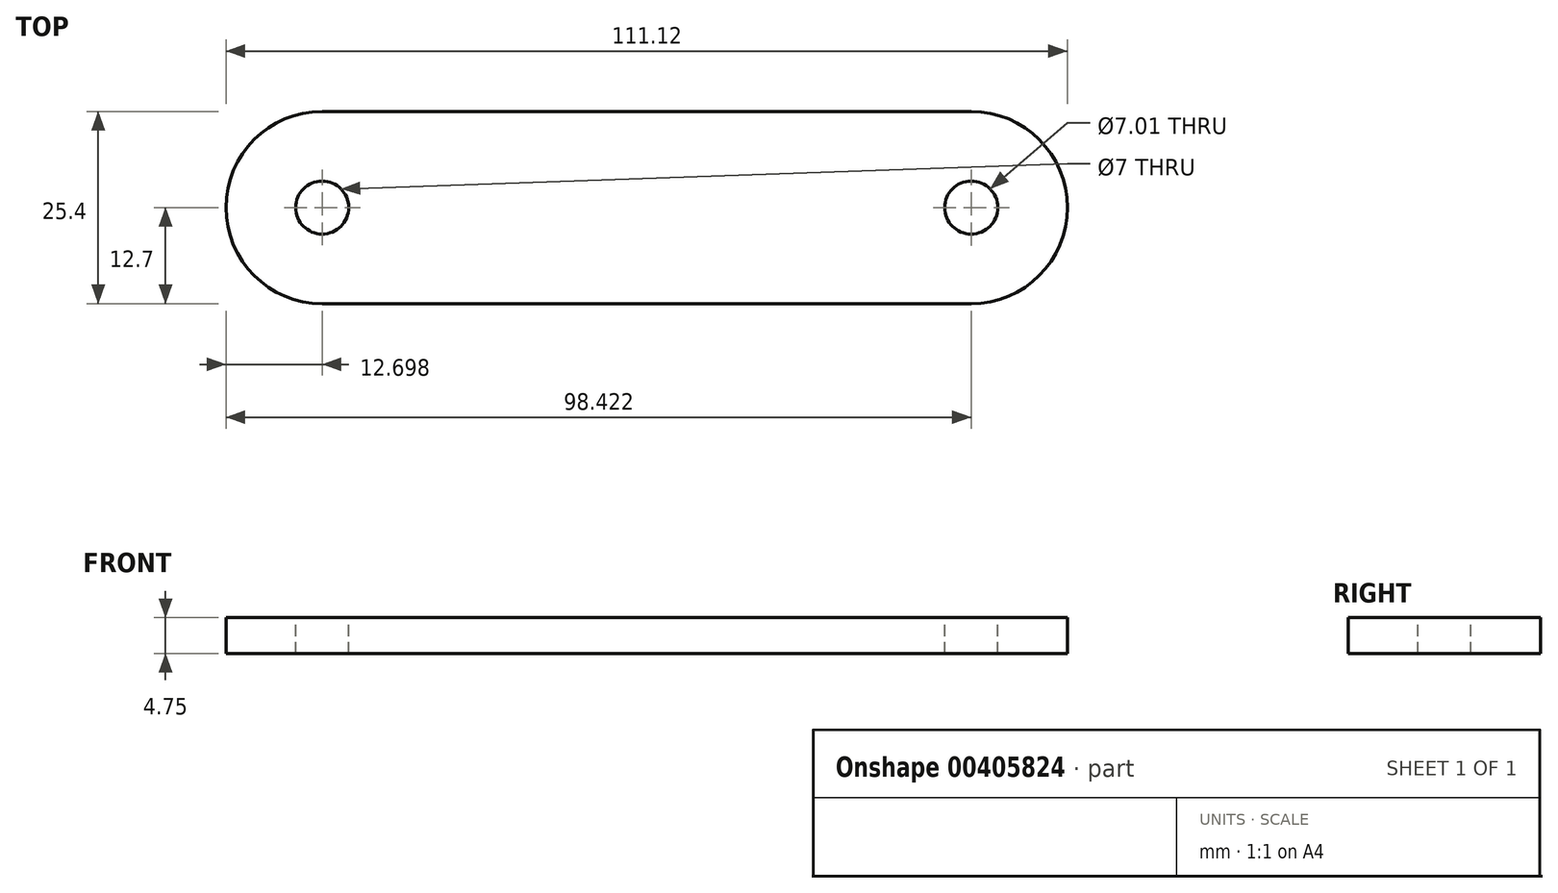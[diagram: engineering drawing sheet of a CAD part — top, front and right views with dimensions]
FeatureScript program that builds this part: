
annotation { "Feature Type Name" : "Feature", "Feature Type Description" : "" }
export const myFeature = defineFeature(function(context is Context, id is Id, definition is map)
    precondition{}
    {
        {
            var Q0;
            Q0=qCreatedBy(makeId("Top.planeOp"),FACE);
            var sketch = newSketch(context, id + "F0", { "sketchPlane" : qUnion([Q0])});
            skLineSegment(sketch, "E0.bottom", {"start": v(55.56, 12.7) * mm, "end": v(-55.56, 12.7) * mm});
            skLineSegment(sketch, "E0.top", {"start": v(55.56, -12.7) * mm, "end": v(-55.56, -12.7) * mm});
            skLineSegment(sketch, "E0.left", {"start": v(55.56, 12.7) * mm, "end": v(55.56, -12.7) * mm});
            skLineSegment(sketch, "E0.right", {"start": v(-55.56, 12.7) * mm, "end": v(-55.56, -12.7) * mm});
            skPoint(sketch, "E0.middle", {"position": v(0, 0) * mm});
            skSolve(sketch);
        }
        {
            var Q0;
            Q0=makeQuery(id+"F0.imprint","IMPRINT",FACE,{"disambiguationData":[TD([[makeQuery(id+"F0.imprint","IMPRINT",EDGE,{"derivedFrom":sQuery(id+"F0.wireOp",EDGE,"E0.bottom")}),1.0]])]});
            extrude(context, id + "F1", {"entities" : qUnion([Q0]), "depth" : 4.75 * mm});
        }
        {
            var Q0;
            Q0=makeQuery(id+"F1.opExtrude","SWEPT_EDGE",EDGE,{"disambiguationData":[OSD([sQuery(id+"F0.wireOp",EDGE,"E0.top"),sQuery(id+"F0.wireOp",EDGE,"E0.right")])]});
            var Q1;
            Q1=makeQuery(id+"F1.opExtrude","SWEPT_EDGE",EDGE,{"disambiguationData":[OSD([sQuery(id+"F0.wireOp",EDGE,"E0.bottom"),sQuery(id+"F0.wireOp",EDGE,"E0.right")])]});
            var Q2;
            Q2=makeQuery(id+"F1.opExtrude","SWEPT_EDGE",EDGE,{"disambiguationData":[OSD([sQuery(id+"F0.wireOp",EDGE,"E0.top"),sQuery(id+"F0.wireOp",EDGE,"E0.left")])]});
            var Q3;
            Q3=makeQuery(id+"F1.opExtrude","SWEPT_EDGE",EDGE,{"disambiguationData":[OSD([sQuery(id+"F0.wireOp",EDGE,"E0.bottom"),sQuery(id+"F0.wireOp",EDGE,"E0.left")])]});
            fillet(context, id + "F2", {"entities" : qUnion([Q0, Q1, Q2, Q3]), "radius" : 12.7 * mm, "tangentPropagation" : true, "allowEdgeOverflow" : false});
        }
        {
            var Q0;
            Q0=makeQuery(id+"F1.opExtrude","CAP_FACE",FACE,{"disambiguationData":[OSD([sQuery(id+"F0.wireOp",EDGE,"E0.bottom"),sQuery(id+"F0.wireOp",EDGE,"E0.top"),sQuery(id+"F0.wireOp",EDGE,"E0.left"),sQuery(id+"F0.wireOp",EDGE,"E0.right")])],"isStart":false});
            var sketch = newSketch(context, id + "F3", { "sketchPlane" : qUnion([Q0])});
            skCircle(sketch, "E1", {"center": v(-42.86, 0) * mm, "radius": 3.5 * mm});
            skCircle(sketch, "E2", {"center": v(42.86, 0) * mm, "radius": 3.5 * mm});
            skSolve(sketch);
        }
        {
            var Q0;
            Q0 = qSketchRegion(id + "F3", true);
            extrude(context, id + "F4", {"entities" : qUnion([Q0]), "operationType" : NewBodyOperationType.REMOVE, "oppositeDirection" : true, "depth" : 25.4 * mm});
        }
    });
